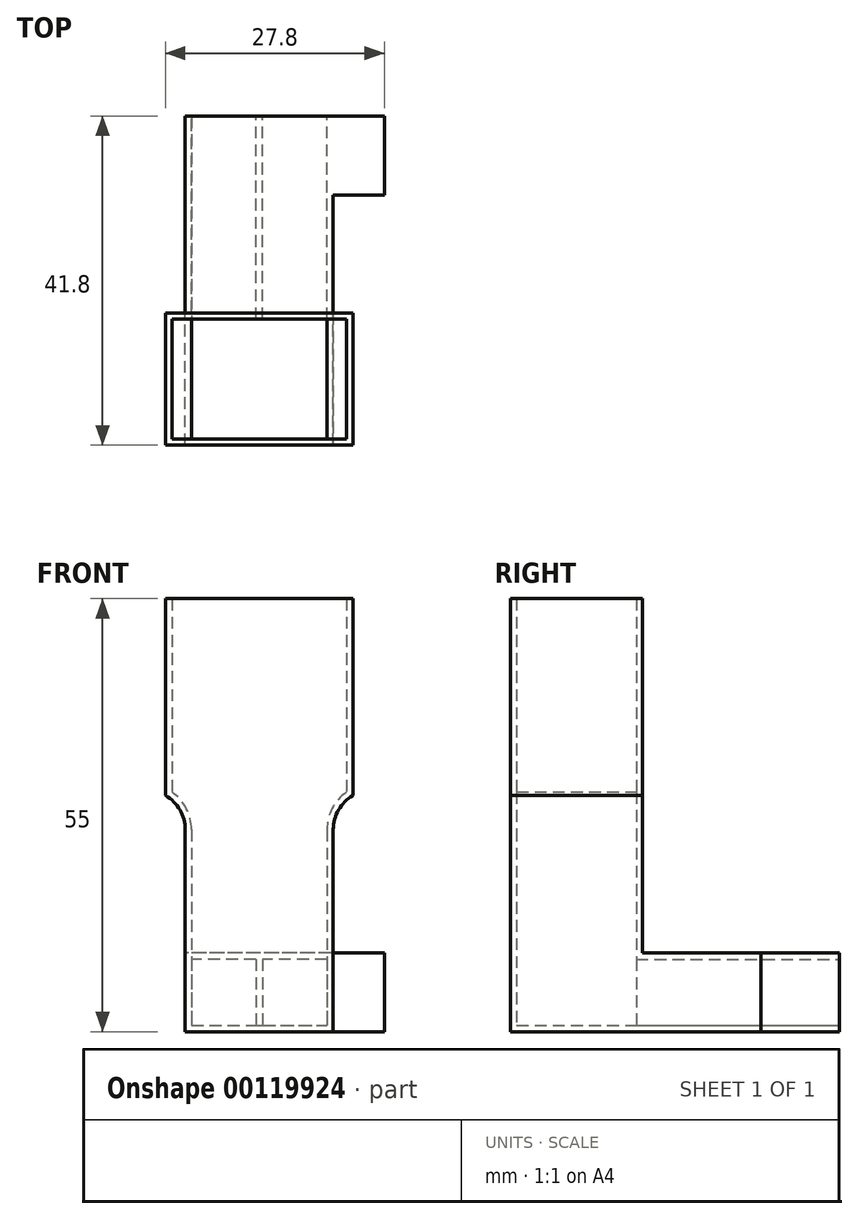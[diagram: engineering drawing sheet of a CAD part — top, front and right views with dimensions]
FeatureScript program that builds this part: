
annotation { "Feature Type Name" : "Feature", "Feature Type Description" : "" }
export const myFeature = defineFeature(function(context is Context, id is Id, definition is map)
    precondition{}
    {
        {
            assignVariable(context, id + "F0", {"name" : "fanMouthDepth", "anyValue" : 15.2});
        }
        {
            assignVariable(context, id + "F1", {"name" : "ductWallThickness", "anyValue" : .8});
        }
        {
            var Q0;
            Q0=qCreatedBy(makeId("Front.planeOp"),FACE);
            var sketch = newSketch(context, id + "F2", { "sketchPlane" : qUnion([Q0])});
            skLineSegment(sketch, "E0.bottom", {"start": v(0, 25) * mm, "end": v(23.8, 25) * mm});
            skLineSegment(sketch, "E0.top", {"start": v(0, 0) * mm, "end": v(23.8, 0) * mm});
            skLineSegment(sketch, "E0.left", {"start": v(0, 25) * mm, "end": v(0, 0) * mm});
            skLineSegment(sketch, "E0.right", {"start": v(23.8, 25) * mm, "end": v(23.8, 0) * mm});
            skLineSegment(sketch, "E1.bottom", {"start": v(2.5, 0) * mm, "end": v(21.3, 0) * mm});
            skLineSegment(sketch, "E1.top", {"start": v(2.5, -30) * mm, "end": v(21.3, -30) * mm});
            skLineSegment(sketch, "E1.left", {"start": v(2.5, 0) * mm, "end": v(2.5, -30) * mm});
            skLineSegment(sketch, "E1.right", {"start": v(21.3, 0) * mm, "end": v(21.3, -30) * mm});
            skPoint(sketch, "E2", {"position": v(11.9, 0) * mm});
            skSolve(sketch);
        }
        {
            var Q0;
            Q0 = qSketchRegion(id + "F2", true);
            extrude(context, id + "F3", {"entities" : qUnion([Q0]), "depth" : (getVariable(context, 'fanMouthDepth') + 2 * getVariable(context, 'ductWallThickness')) * mm});
        }
        {
            var Q0;
            Q0=makeQuery(id+"F3.opExtrude","SWEPT_EDGE",EDGE,{"disambiguationData":[OSD([sQuery(id+"F2.wireOp",EDGE,"E0.top"),sQuery(id+"F2.wireOp",EDGE,"E1.bottom"),sQuery(id+"F2.wireOp",EDGE,"E1.left")])]});
            var Q1;
            Q1=makeQuery(id+"F3.opExtrude","SWEPT_EDGE",EDGE,{"disambiguationData":[OSD([sQuery(id+"F2.wireOp",EDGE,"E0.top"),sQuery(id+"F2.wireOp",EDGE,"E1.bottom"),sQuery(id+"F2.wireOp",EDGE,"E1.right")])]});
            fillet(context, id + "F4", {"entities" : qUnion([Q0, Q1]), "radius" : 5 * mm, "tangentPropagation" : true, "allowEdgeOverflow" : false});
        }
        {
            var Q0;
            Q0=makeQuery(id+"F3.opExtrude","SWEPT_FACE",FACE,{"disambiguationData":[OSD([sQuery(id+"F2.wireOp",EDGE,"E0.bottom")])]});
            shell(context, id + "F5", {"entities" : qUnion([Q0]), "thickness" : (getVariable(context, 'ductWallThickness')) * mm});
        }
        {
            var Q0;
            Q0=makeQuery(id+"F3.opExtrude","CAP_FACE",FACE,{"disambiguationData":[OSD([sQuery(id+"F2.wireOp",EDGE,"E0.bottom"),sQuery(id+"F2.wireOp",EDGE,"E0.top"),sQuery(id+"F2.wireOp",EDGE,"E0.left"),sQuery(id+"F2.wireOp",EDGE,"E0.right"),sQuery(id+"F2.wireOp",EDGE,"E1.top"),sQuery(id+"F2.wireOp",EDGE,"E1.left"),sQuery(id+"F2.wireOp",EDGE,"E1.right")])],"isStart":true});
            var sketch = newSketch(context, id + "F6", { "sketchPlane" : qUnion([Q0])});
            skLineSegment(sketch, "E3.bottom", {"start": v(-21.3, -30) * mm, "end": v(-2.5, -30) * mm});
            skLineSegment(sketch, "E3.top", {"start": v(-21.3, -20) * mm, "end": v(-2.5, -20) * mm});
            skLineSegment(sketch, "E3.left", {"start": v(-21.3, -30) * mm, "end": v(-21.3, -20) * mm});
            skLineSegment(sketch, "E3.right", {"start": v(-2.5, -30) * mm, "end": v(-2.5, -20) * mm});
            skSolve(sketch);
        }
        {
            var Q0;
            Q0 = qSketchRegion(id + "F6", true);
            extrude(context, id + "F7", {"entities" : qUnion([Q0]), "operationType" : NewBodyOperationType.ADD, "depth" : 25 * mm});
        }
        {
            var Q0;
            Q0=makeQuery(id+"F7.opExtrude","CAP_FACE",FACE,{"disambiguationData":[OSD([sQuery(id+"F6.wireOp",EDGE,"E3.bottom"),sQuery(id+"F6.wireOp",EDGE,"E3.top"),sQuery(id+"F6.wireOp",EDGE,"E3.left"),sQuery(id+"F6.wireOp",EDGE,"E3.right")])],"isStart":false});
            shell(context, id + "F8", {"entities" : qUnion([Q0]), "thickness" : (getVariable(context, 'ductWallThickness')) * mm});
        }
        {
            var Q0;
            Q0=makeQuery(id+"F8.opShell","OFFSET_FACE",FACE,{"disambiguationData":[OSD([sQuery(id+"F2.wireOp",EDGE,"E0.bottom"),sQuery(id+"F2.wireOp",EDGE,"E0.top"),sQuery(id+"F2.wireOp",EDGE,"E0.left"),sQuery(id+"F2.wireOp",EDGE,"E0.right"),sQuery(id+"F2.wireOp",EDGE,"E1.top"),sQuery(id+"F2.wireOp",EDGE,"E1.left"),sQuery(id+"F2.wireOp",EDGE,"E1.right")])]});
            extrude(context, id + "F9", {"entities" : qUnion([Q0]), "operationType" : NewBodyOperationType.REMOVE, "endBound" : BoundingType.UP_TO_NEXT, "oppositeDirection" : true, "depth" : 25 * mm});
        }
        {
            var Q0;
            Q0=makeQuery(id+"F7.opExtrude","CAP_FACE",FACE,{"disambiguationData":[OSD([sQuery(id+"F6.wireOp",EDGE,"E3.bottom"),sQuery(id+"F6.wireOp",EDGE,"E3.top"),sQuery(id+"F6.wireOp",EDGE,"E3.left"),sQuery(id+"F6.wireOp",EDGE,"E3.right")])],"isStart":false});
            var sketch = newSketch(context, id + "F10", { "sketchPlane" : qUnion([Q0])});
            skLineSegment(sketch, "E4.bottom", {"start": v(-12.3, -20.8) * mm, "end": v(-11.5, -20.8) * mm});
            skLineSegment(sketch, "E4.top", {"start": v(-12.3, -29.2) * mm, "end": v(-11.5, -29.2) * mm});
            skLineSegment(sketch, "E4.left", {"start": v(-12.3, -20.8) * mm, "end": v(-12.3, -29.2) * mm});
            skLineSegment(sketch, "E4.right", {"start": v(-11.5, -20.8) * mm, "end": v(-11.5, -29.2) * mm});
            skPoint(sketch, "E5", {"position": v(-11.9, -20.8) * mm});
            skSolve(sketch);
        }
        {
            var Q0;
            Q0 = qSketchRegion(id + "F10", true);
            var Q1;
            {var subQ0=sQuery(id+"F2.wireOp",EDGE,"E1.right");var subQ1=sQuery(id+"F2.wireOp",EDGE,"E1.left");var subQ2=sQuery(id+"F2.wireOp",EDGE,"E1.top");var subQ3=sQuery(id+"F2.wireOp",EDGE,"E0.right");var subQ4=sQuery(id+"F2.wireOp",EDGE,"E0.left");var subQ5=sQuery(id+"F2.wireOp",EDGE,"E0.top");var subQ6=sQuery(id+"F2.wireOp",EDGE,"E0.bottom");Q1=makeQuery(id+"F5.opShell","OFFSET_FACE",FACE,{"disambiguationData":[OSD([subQ6,subQ5,subQ4,subQ3,subQ2,subQ1,subQ0]),TDD([makeQuery(id+"F3.opExtrude","CAP_FACE",FACE,{"disambiguationData":[OSD([subQ6,subQ5,subQ4,subQ3,subQ2,subQ1,subQ0])],"isStart":true})])]});}
            extrude(context, id + "F11", {"entities" : qUnion([Q0]), "operationType" : NewBodyOperationType.ADD, "endBound" : BoundingType.UP_TO_SURFACE, "oppositeDirection" : true, "endBoundEntityFace" : qUnion([Q1]), "depth" : 25 * mm});
        }
        {
            var Q0;
            Q0=makeQuery(id+"F7.boolean.opBoolean","MERGE",FACE,{"derivedFrom":[makeQuery(id+"F3.opExtrude","SWEPT_FACE",FACE,{"disambiguationData":[OSD([sQuery(id+"F2.wireOp",EDGE,"E1.right")])]}),makeQuery(id+"F7.opExtrude","SWEPT_FACE",FACE,{"disambiguationData":[OSD([sQuery(id+"F6.wireOp",EDGE,"E3.left")])]})]});
            var sketch = newSketch(context, id + "F12", { "sketchPlane" : qUnion([Q0])});
            skLineSegment(sketch, "E6.bottom", {"start": v(15, -20) * mm, "end": v(25, -20) * mm});
            skLineSegment(sketch, "E6.top", {"start": v(15, -30) * mm, "end": v(25, -30) * mm});
            skLineSegment(sketch, "E6.left", {"start": v(15, -20) * mm, "end": v(15, -30) * mm});
            skLineSegment(sketch, "E6.right", {"start": v(25, -20) * mm, "end": v(25, -30) * mm});
            skSolve(sketch);
        }
        {
            var Q0;
            Q0=makeQuery(id+"F12.imprint","IMPRINT",FACE,{"disambiguationData":[TD([[makeQuery(id+"F12.imprint","IMPRINT",EDGE,{"derivedFrom":sQuery(id+"F12.wireOp",EDGE,"E6.bottom")}),1.0]])]});
            extrude(context, id + "F13", {"entities" : qUnion([Q0]), "operationType" : NewBodyOperationType.ADD, "depth" : 6.5 * mm});
        }
    });
